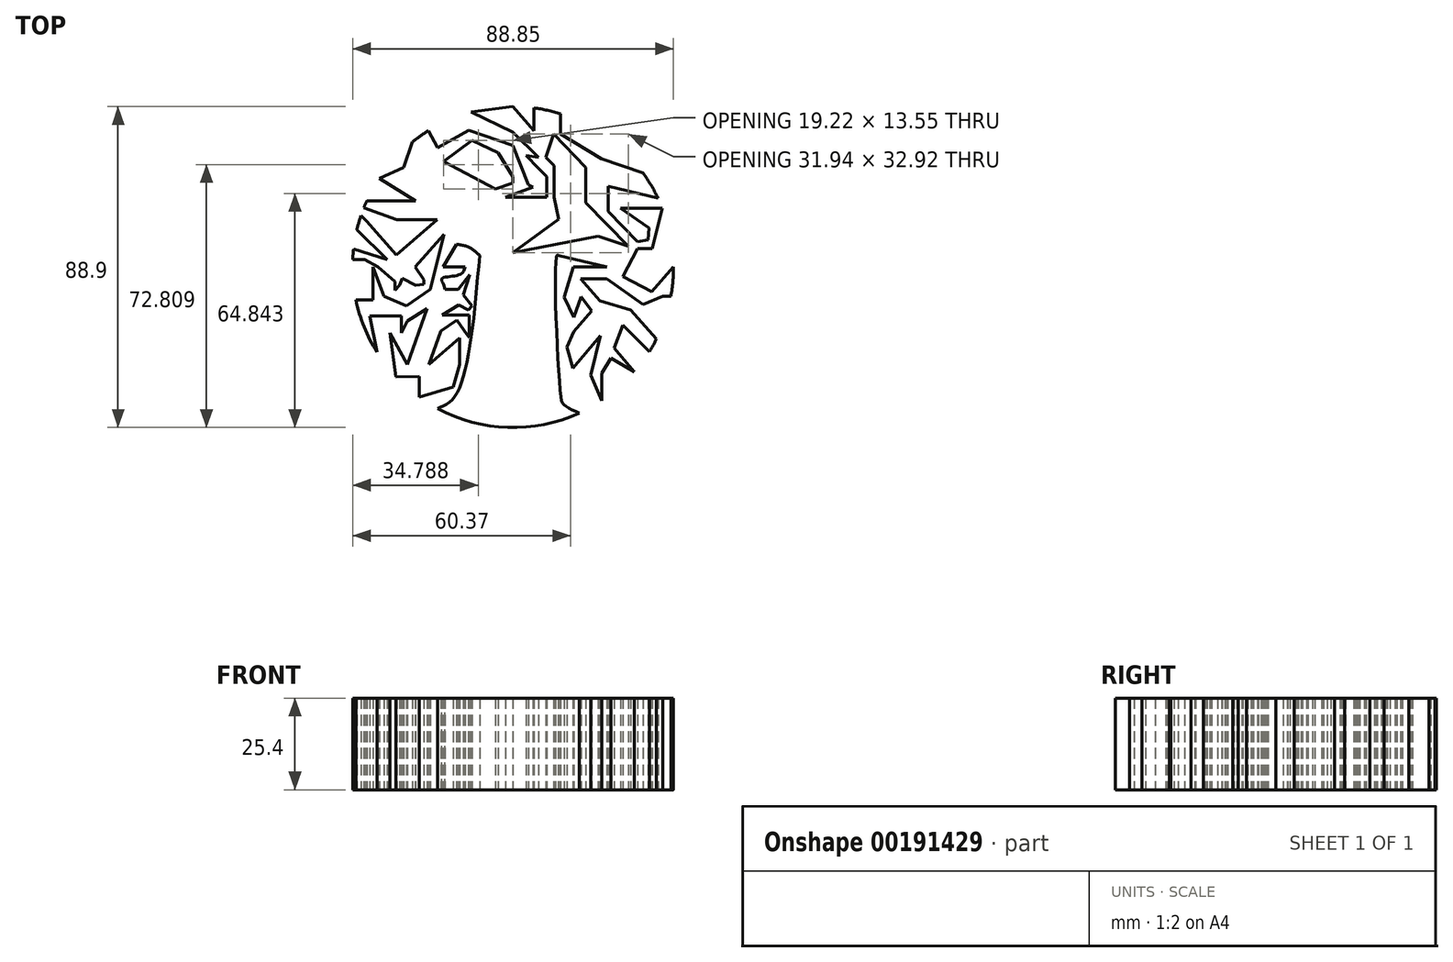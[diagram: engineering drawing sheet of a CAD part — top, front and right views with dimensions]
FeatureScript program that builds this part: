
annotation { "Feature Type Name" : "Feature", "Feature Type Description" : "" }
export const myFeature = defineFeature(function(context is Context, id is Id, definition is map)
    precondition{}
    {
        {
            var Q0;
            Q0=qCreatedBy(makeId("Top.planeOp"),FACE);
            var sketch = newSketch(context, id + "F0", { "sketchPlane" : qUnion([Q0])});
            skCircle(sketch, "E0", {"center": v(0, 0) * mm, "radius": 44.45 * mm});
            skFitSpline(sketch, "E1", {"points": [v(-20.9, -39.23) * mm, v(-15.64, -35.1) * mm, v(-9.26, 3.2) * mm], "startDerivative": vector(19.18, 8.13) * mm, "endDerivative": vector(5.89, 68.32) * mm});
            skFitSpline(sketch, "E2", {"points": [v(18.34, -40.5) * mm, v(14.4, -38.44) * mm, v(13.17, -35.1) * mm, v(12.14, 3.2) * mm, v(12.56, 3.2) * mm], "startDerivative": vector(-23.7, 11.14) * mm, "endDerivative": vector(7.4, -4.86) * mm});
            skFitSpline(sketch, "E3", {"points": [v(-9.26, 3.2) * mm, v(-12.14, 5.45) * mm, v(-15.64, 6.28) * mm], "startDerivative": vector(-5.4, 5.22) * mm, "endDerivative": vector(-7.35, 0.95) * mm});
            skFitSpline(sketch, "E4", {"points": [v(-3.09, 4.07) * mm, v(-3.91, 5.45) * mm, v(-7.4, 8.13) * mm, v(-12.14, 9.78) * mm], "startDerivative": vector(-2.6, 5.77) * mm, "endDerivative": vector(-12.06, 3.2) * mm});
            skLineSegment(sketch, "E5", {"start": v(-15.64, 6.28) * mm, "end": v(-19.4, 0) * mm});
            skLineSegment(sketch, "E6", {"start": v(-19.4, 0) * mm, "end": v(-15.64, 6.28) * mm});
            skLineSegment(sketch, "E7", {"start": v(-19.11, 9) * mm, "end": v(-22.86, -6.18) * mm});
            skLineSegment(sketch, "E8", {"start": v(-19.4, 0) * mm, "end": v(-13.2, 0) * mm});
            skFitSpline(sketch, "E9", {"points": [v(-13.2, 0) * mm, v(-14.9, -2.14) * mm, v(-19.75, -3.28) * mm, v(-18.9, -6.18) * mm], "startDerivative": vector(-3.74, -8.86) * mm, "endDerivative": vector(-0.76, -11.72) * mm});
            skLineSegment(sketch, "E10", {"start": v(-22.86, -6.18) * mm, "end": v(-29.5, -10.8) * mm});
            skLineSegment(sketch, "E11", {"start": v(-23.82, -11.53) * mm, "end": v(-29.28, -14.96) * mm});
            skLineSegment(sketch, "E12", {"start": v(-29.28, -14.96) * mm, "end": v(-30.9, -18.22) * mm});
            skLineSegment(sketch, "E13", {"start": v(-30.9, -18.22) * mm, "end": v(-30.9, -13.53) * mm});
            skLineSegment(sketch, "E14", {"start": v(-23.82, -11.53) * mm, "end": v(-29.28, -26.96) * mm});
            skLineSegment(sketch, "E15", {"start": v(-18.9, -6.18) * mm, "end": v(-15.19, -6.18) * mm});
            skLineSegment(sketch, "E16", {"start": v(-19.62, -13.24) * mm, "end": v(-15.05, -10.53) * mm});
            skLineSegment(sketch, "E17", {"start": v(-15.19, -6.18) * mm, "end": v(-12.01, -2.14) * mm});
            skLineSegment(sketch, "E18", {"start": v(-13.83, -7.72) * mm, "end": v(-12.01, -2.14) * mm});
            skLineSegment(sketch, "E19", {"start": v(-13.83, -7.72) * mm, "end": v(-11.33, -10.77) * mm});
            skLineSegment(sketch, "E20", {"start": v(-15.05, -10.53) * mm, "end": v(-12.34, -11.88) * mm});
            skPoint(sketch, "E20.endSnap0", {"position": v(-17.33, -11.88) * mm});
            skLineSegment(sketch, "E21", {"start": v(-12.34, -11.88) * mm, "end": v(-11.33, -10.77) * mm});
            skLineSegment(sketch, "E22", {"start": v(-19.62, -13.24) * mm, "end": v(-12.16, -13.24) * mm});
            skLineSegment(sketch, "E23", {"start": v(-12.16, -13.24) * mm, "end": v(-12.16, -19.5) * mm});
            skLineSegment(sketch, "E24", {"start": v(-12.16, -19.5) * mm, "end": v(-13.58, -17.67) * mm});
            skLineSegment(sketch, "E25", {"start": v(-13.58, -17.67) * mm, "end": v(-15.55, -14.75) * mm});
            skLineSegment(sketch, "E26", {"start": v(-29.5, -10.8) * mm, "end": v(-35.8, -8.08) * mm});
            skLineSegment(sketch, "E27", {"start": v(-30.9, -13.53) * mm, "end": v(-39.68, -13.53) * mm});
            skLineSegment(sketch, "E28", {"start": v(-35.8, -8.08) * mm, "end": v(-38.85, 0) * mm});
            skLineSegment(sketch, "E29", {"start": v(-38.85, 0) * mm, "end": v(-38.85, -9.05) * mm});
            skLineSegment(sketch, "E30", {"start": v(-38.85, -9.05) * mm, "end": v(-43.52, -9.05) * mm});
            skLineSegment(sketch, "E31", {"start": v(-39.68, -13.53) * mm, "end": v(-37.68, -23.58) * mm});
            skLineSegment(sketch, "E32", {"start": v(-29.28, -26.96) * mm, "end": v(-34.07, -18.22) * mm});
            skLineSegment(sketch, "E33", {"start": v(-34.07, -18.22) * mm, "end": v(-32.42, -30.41) * mm});
            skLineSegment(sketch, "E34", {"start": v(-15.55, -14.75) * mm, "end": v(-20, -17.75) * mm});
            skLineSegment(sketch, "E35", {"start": v(-20, -17.75) * mm, "end": v(-23.26, -26.96) * mm});
            skLineSegment(sketch, "E36", {"start": v(-23.26, -26.96) * mm, "end": v(-14.85, -19.68) * mm});
            skLineSegment(sketch, "E37", {"start": v(-14.85, -19.68) * mm, "end": v(-14.85, -26.96) * mm});
            skLineSegment(sketch, "E38", {"start": v(-14.85, -26.96) * mm, "end": v(-16.63, -33.3) * mm});
            skLineSegment(sketch, "E39", {"start": v(-16.63, -33.3) * mm, "end": v(-26.03, -36.03) * mm});
            skLineSegment(sketch, "E40", {"start": v(-26.03, -36.03) * mm, "end": v(-26.03, -30.33) * mm});
            skLineSegment(sketch, "E41", {"start": v(-26.03, -30.33) * mm, "end": v(-32.42, -30.41) * mm});
            skLineSegment(sketch, "E42", {"start": v(-19.11, 9) * mm, "end": v(-27.13, 0) * mm});
            skLineSegment(sketch, "E43", {"start": v(-27.13, 0) * mm, "end": v(-24.68, -3.52) * mm});
            skLineSegment(sketch, "E44", {"start": v(-30.62, -3.12) * mm, "end": v(-26.93, -5) * mm});
            skLineSegment(sketch, "E45", {"start": v(-24.65, -4.78) * mm, "end": v(-26.93, -5) * mm});
            skLineSegment(sketch, "E46", {"start": v(-24.65, -4.78) * mm, "end": v(-24.68, -3.52) * mm});
            skLineSegment(sketch, "E47", {"start": v(-31.4, -5) * mm, "end": v(-30.62, -3.12) * mm});
            skLineSegment(sketch, "E48", {"start": v(-32.65, -6.5) * mm, "end": v(-31.4, -5) * mm});
            skPoint(sketch, "E48.startSnap0", {"position": v(-32.65, -9.43) * mm});
            skLineSegment(sketch, "E49", {"start": v(-32.65, -6.5) * mm, "end": v(-32.65, -4.06) * mm});
            skLineSegment(sketch, "E50", {"start": v(-32.65, -4.06) * mm, "end": v(-37.33, 0) * mm});
            skPoint(sketch, "E50.endSnap0", {"position": v(-37.33, -4.04) * mm});
            skLineSegment(sketch, "E51", {"start": v(-37.33, 0) * mm, "end": v(-41.1, 2.03) * mm});
            skLineSegment(sketch, "E52", {"start": v(-41.1, 2.03) * mm, "end": v(-44.4, 2.03) * mm});
            skLineSegment(sketch, "E53", {"start": v(-44.17, 4.98) * mm, "end": v(-34.9, 2.03) * mm});
            skLineSegment(sketch, "E54", {"start": v(-34.9, 2.03) * mm, "end": v(-43.25, 10.27) * mm});
            skLineSegment(sketch, "E55", {"start": v(-40.55, 12.7) * mm, "end": v(-42.09, 14.3) * mm});
            skLineSegment(sketch, "E56", {"start": v(-42.09, 14.3) * mm, "end": v(-40.55, 12.7) * mm});
            skLineSegment(sketch, "E57", {"start": v(-40.55, 12.7) * mm, "end": v(-32.33, 3.28) * mm});
            skLineSegment(sketch, "E58", {"start": v(-32.33, 3.28) * mm, "end": v(-20.99, 13.18) * mm});
            skPoint(sketch, "E58.endSnap0", {"position": v(-20.99, 1.4) * mm});
            skLineSegment(sketch, "E59", {"start": v(-20.99, 13.18) * mm, "end": v(-32.22, 13.18) * mm});
            skLineSegment(sketch, "E60", {"start": v(-12.14, 9.78) * mm, "end": v(-22.5, 17.51) * mm});
            skLineSegment(sketch, "E61", {"start": v(-22.5, 17.51) * mm, "end": v(-20.99, 24.66) * mm});
            skLineSegment(sketch, "E62", {"start": v(-32.22, 13.18) * mm, "end": v(-41.3, 16.41) * mm});
            skLineSegment(sketch, "E63", {"start": v(-26.96, 18.32) * mm, "end": v(-40.5, 18.32) * mm});
            skLineSegment(sketch, "E64", {"start": v(-40.5, 18.32) * mm, "end": v(-26.96, 18.32) * mm});
            skLineSegment(sketch, "E65", {"start": v(-26.96, 18.32) * mm, "end": v(-37.03, 24.6) * mm});
            skLineSegment(sketch, "E66", {"start": v(-37.03, 24.6) * mm, "end": v(-30.35, 27.62) * mm});
            skLineSegment(sketch, "E67", {"start": v(-30.35, 27.62) * mm, "end": v(-27.85, 34.64) * mm});
            skLineSegment(sketch, "E68", {"start": v(-17.17, 23.25) * mm, "end": v(-20.99, 24.66) * mm});
            skLineSegment(sketch, "E69", {"start": v(-19.22, 29.25) * mm, "end": v(-4.92, 21.58) * mm});
            skLineSegment(sketch, "E70", {"start": v(-4.92, 21.58) * mm, "end": v(0, 23.25) * mm});
            skLineSegment(sketch, "E71", {"start": v(-17.17, 23.25) * mm, "end": v(-4.92, 16.69) * mm});
            skLineSegment(sketch, "E72", {"start": v(-4.92, 16.69) * mm, "end": v(-4.92, 13.07) * mm});
            skLineSegment(sketch, "E73", {"start": v(-4.92, 13.07) * mm, "end": v(0, 16.69) * mm});
            skLineSegment(sketch, "E74", {"start": v(0, 16.69) * mm, "end": v(9.33, 16.69) * mm});
            skLineSegment(sketch, "E75", {"start": v(9.33, 16.69) * mm, "end": v(0, 16.69) * mm});
            skLineSegment(sketch, "E76", {"start": v(-2.1, 19.37) * mm, "end": v(5.57, 22.1) * mm});
            skLineSegment(sketch, "E77", {"start": v(-2.1, 19.37) * mm, "end": v(9.33, 19.37) * mm});
            skLineSegment(sketch, "E78", {"start": v(9.33, 19.37) * mm, "end": v(-2.1, 19.37) * mm});
            skLineSegment(sketch, "E79", {"start": v(0, 25.08) * mm, "end": v(0, 23.25) * mm});
            skLineSegment(sketch, "E80", {"start": v(-19.22, 29.25) * mm, "end": v(-11.4, 35.13) * mm});
            skLineSegment(sketch, "E81", {"start": v(-20.82, 33.06) * mm, "end": v(-12.26, 37.91) * mm});
            skLineSegment(sketch, "E82", {"start": v(-20.82, 33.06) * mm, "end": v(-23.48, 37.74) * mm});
            skLineSegment(sketch, "E83", {"start": v(-11.4, 35.13) * mm, "end": v(-4.13, 31.66) * mm});
            skLineSegment(sketch, "E84", {"start": v(0, 25.08) * mm, "end": v(-4.13, 31.66) * mm});
            skLineSegment(sketch, "E85", {"start": v(4.22, 22.78) * mm, "end": v(5.57, 22.1) * mm});
            skLineSegment(sketch, "E86", {"start": v(4.22, 22.78) * mm, "end": v(0, 33.63) * mm});
            skLineSegment(sketch, "E87", {"start": v(0, 33.63) * mm, "end": v(-12.26, 37.91) * mm});
            skLineSegment(sketch, "E88", {"start": v(-3.28, 4.5) * mm, "end": v(0, 9.83) * mm});
            skLineSegment(sketch, "E89", {"start": v(0, 9.83) * mm, "end": v(9.33, 16.69) * mm});
            skLineSegment(sketch, "E90", {"start": v(9.33, 19.37) * mm, "end": v(9.33, 25.03) * mm});
            skLineSegment(sketch, "E91", {"start": v(11.38, 19.37) * mm, "end": v(11.38, 28.14) * mm});
            skLineSegment(sketch, "E92", {"start": v(11.38, 28.14) * mm, "end": v(9.03, 30.39) * mm});
            skLineSegment(sketch, "E93", {"start": v(9.03, 30.39) * mm, "end": v(11.3, 36.85) * mm});
            skLineSegment(sketch, "E94", {"start": v(9.33, 25.03) * mm, "end": v(7.06, 27.35) * mm});
            skLineSegment(sketch, "E95", {"start": v(7.06, 27.35) * mm, "end": v(3.65, 30.9) * mm});
            skLineSegment(sketch, "E96", {"start": v(3.65, 30.9) * mm, "end": v(7.06, 30.39) * mm});
            skLineSegment(sketch, "E97", {"start": v(7.06, 30.39) * mm, "end": v(0, 37.37) * mm});
            skLineSegment(sketch, "E98", {"start": v(0, 3.93) * mm, "end": v(12.69, 13.26) * mm});
            skPoint(sketch, "E98.endSnap0", {"position": v(4.67, 13.26) * mm});
            skLineSegment(sketch, "E99", {"start": v(12.69, 13.26) * mm, "end": v(11.38, 19.37) * mm});
            skLineSegment(sketch, "E100", {"start": v(0, 37.37) * mm, "end": v(-11.57, 42.92) * mm});
            skLineSegment(sketch, "E101", {"start": v(-11.57, 42.92) * mm, "end": v(0, 44.45) * mm});
            skLineSegment(sketch, "E102", {"start": v(0, 44.45) * mm, "end": v(5.82, 37.78) * mm});
            skLineSegment(sketch, "E103", {"start": v(5.82, 37.78) * mm, "end": v(5.82, 44.07) * mm});
            skPoint(sketch, "E104.endSnap0", {"position": v(6.34, 8.6) * mm});
            skLineSegment(sketch, "E105", {"start": v(23.57, 8.6) * mm, "end": v(0, 3.93) * mm});
            skLineSegment(sketch, "E106", {"start": v(11.3, 36.85) * mm, "end": v(20.16, 27.61) * mm});
            skLineSegment(sketch, "E107", {"start": v(20.16, 27.61) * mm, "end": v(20.16, 17.86) * mm});
            skLineSegment(sketch, "E108", {"start": v(13.15, 42.46) * mm, "end": v(13.15, 36.85) * mm});
            skLineSegment(sketch, "E109", {"start": v(13.15, 36.85) * mm, "end": v(24.5, 30.05) * mm});
            skLineSegment(sketch, "E110", {"start": v(24.5, 30.05) * mm, "end": v(36.01, 26.06) * mm});
            skLineSegment(sketch, "E111", {"start": v(36.01, 26.06) * mm, "end": v(36.01, 26.06) * mm});
            skLineSegment(sketch, "E112", {"start": v(26.36, 22.37) * mm, "end": v(26.36, 15.34) * mm});
            skLineSegment(sketch, "E113", {"start": v(26.36, 15.34) * mm, "end": v(34.46, 7) * mm});
            skLineSegment(sketch, "E114", {"start": v(26.36, 22.37) * mm, "end": v(40.15, 19.07) * mm});
            skLineSegment(sketch, "E115", {"start": v(20.16, 17.86) * mm, "end": v(31.94, 5.74) * mm});
            skLineSegment(sketch, "E116", {"start": v(37.35, 7.46) * mm, "end": v(37.66, 10.8) * mm});
            skLineSegment(sketch, "E117", {"start": v(37.35, 7.46) * mm, "end": v(34.46, 7) * mm});
            skLineSegment(sketch, "E118", {"start": v(37.66, 10.8) * mm, "end": v(29.76, 16.33) * mm});
            skLineSegment(sketch, "E119", {"start": v(29.76, 16.33) * mm, "end": v(41.34, 16.33) * mm});
            skLineSegment(sketch, "E120", {"start": v(41.34, 16.33) * mm, "end": v(38.54, 5.1) * mm});
            skLineSegment(sketch, "E121", {"start": v(38.54, 5.1) * mm, "end": v(34.46, 5.1) * mm});
            skLineSegment(sketch, "E122", {"start": v(34.46, 5.1) * mm, "end": v(30.41, -2.57) * mm});
            skLineSegment(sketch, "E123", {"start": v(30.41, -2.57) * mm, "end": v(39.2, 0) * mm});
            skLineSegment(sketch, "E124", {"start": v(39.2, 0) * mm, "end": v(44.36, 2.87) * mm});
            skPoint(sketch, "E124.endSnap0", {"position": v(28.99, 2.87) * mm});
            skLineSegment(sketch, "E125", {"start": v(26.03, 0) * mm, "end": v(16.67, 0) * mm});
            skLineSegment(sketch, "E126", {"start": v(16.67, 0) * mm, "end": v(14.12, -8.3) * mm});
            skPoint(sketch, "E126.endSnap0", {"position": v(14.12, 4.3) * mm});
            skLineSegment(sketch, "E127", {"start": v(26.03, -3.27) * mm, "end": v(18.79, -3.27) * mm});
            skLineSegment(sketch, "E128", {"start": v(18.79, -3.27) * mm, "end": v(24.1, -9.31) * mm});
            skLineSegment(sketch, "E129", {"start": v(26.03, -3.27) * mm, "end": v(36, -10.37) * mm});
            skLineSegment(sketch, "E130", {"start": v(30.41, -2.57) * mm, "end": v(38.38, -6.77) * mm});
            skLineSegment(sketch, "E131", {"start": v(38.38, -6.77) * mm, "end": v(44.45, 0) * mm});
            skLineSegment(sketch, "E132", {"start": v(43.7, -8.1) * mm, "end": v(41.41, -8.1) * mm});
            skPoint(sketch, "E132.endSnap0", {"position": v(41.41, -3.38) * mm});
            skLineSegment(sketch, "E133", {"start": v(36, -10.37) * mm, "end": v(41.41, -8.1) * mm});
            skLineSegment(sketch, "E134", {"start": v(18.87, -8.19) * mm, "end": v(16.8, -14) * mm});
            skLineSegment(sketch, "E135", {"start": v(24.1, -9.31) * mm, "end": v(32.55, -11.92) * mm});
            skLineSegment(sketch, "E136", {"start": v(32.55, -11.92) * mm, "end": v(39.71, -19.97) * mm});
            skLineSegment(sketch, "E137", {"start": v(14.12, -8.3) * mm, "end": v(16.8, -14) * mm});
            skLineSegment(sketch, "E138", {"start": v(18.87, -8.19) * mm, "end": v(21.77, -12.13) * mm});
            skLineSegment(sketch, "E139", {"start": v(21.77, -12.13) * mm, "end": v(16.8, -17.93) * mm});
            skLineSegment(sketch, "E140", {"start": v(16.8, -17.93) * mm, "end": v(14.51, -23.11) * mm});
            skLineSegment(sketch, "E141", {"start": v(30.47, -16.07) * mm, "end": v(37.78, -23.43) * mm});
            skLineSegment(sketch, "E142", {"start": v(30.47, -16.07) * mm, "end": v(27.99, -22.5) * mm});
            skLineSegment(sketch, "E143", {"start": v(27.99, -22.5) * mm, "end": v(33.62, -29.07) * mm});
            skLineSegment(sketch, "E144", {"start": v(33.62, -29.07) * mm, "end": v(27.16, -25.19) * mm});
            skLineSegment(sketch, "E145", {"start": v(27.16, -25.19) * mm, "end": v(24.63, -29.4) * mm});
            skLineSegment(sketch, "E146", {"start": v(24.63, -29.4) * mm, "end": v(24.63, -37) * mm});
            skLineSegment(sketch, "E147", {"start": v(24.63, -37) * mm, "end": v(21.56, -29.96) * mm});
            skLineSegment(sketch, "E148", {"start": v(21.56, -29.96) * mm, "end": v(24.26, -18.97) * mm});
            skLineSegment(sketch, "E149", {"start": v(24.26, -18.97) * mm, "end": v(16.58, -28.1) * mm});
            skLineSegment(sketch, "E150", {"start": v(16.58, -28.1) * mm, "end": v(14.72, -21.46) * mm});
            skLineSegment(sketch, "E151", {"start": v(12.56, 3.2) * mm, "end": v(26.03, 0) * mm});
            skLineSegment(sketch, "E152", {"start": v(23.57, 8.6) * mm, "end": v(31.94, 5.74) * mm});
            skSolve(sketch);
        }
        {
            var Q0;
            {var subQ16=sQuery(id+"F0.wireOp",EDGE,"E1");Q0=makeQuery(id+"F0.imprint","IMPRINT",FACE,{"disambiguationData":[TD([[makeQuery(id+"F0.imprint","IMPRINT",EDGE,{"derivedFrom":subQ16}),-1.0]])]});}
            extrude(context, id + "F1", {"entities" : qUnion([Q0]), "depth" : 25.4 * mm});
        }
    });
